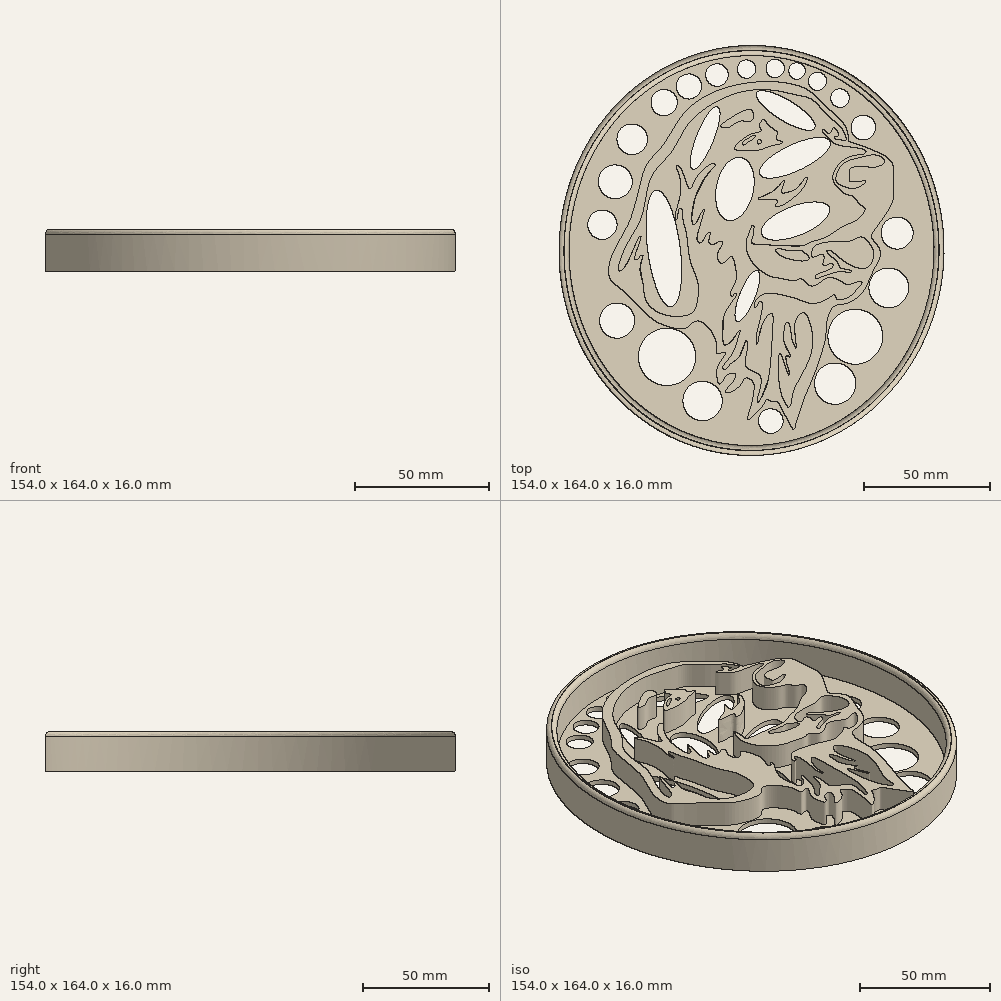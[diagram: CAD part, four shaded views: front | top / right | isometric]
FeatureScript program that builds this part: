
annotation { "Feature Type Name" : "Feature", "Feature Type Description" : "" }
export const myFeature = defineFeature(function(context is Context, id is Id, definition is map)
    precondition{}
    {
        {
            var Q0;
            Q0=qCreatedBy(makeId("Top.planeOp"),FACE);
            var sketch = newSketch(context, id + "F0", { "sketchPlane" : qUnion([Q0])});
            skFitSpline(sketch, "E0", {"points": [v(-56.75, 10.38) * mm, v(-55.7, 19.45) * mm, v(-48.18, 34.24) * mm, v(-42.3, 54.64) * mm, v(-35.83, 62.6) * mm, v(-26.27, 76.78) * mm, v(-4.51, 87.78) * mm, v(20.84, 86.33) * mm, v(30.15, 78.54) * mm, v(37.86, 70.18) * mm, v(38.92, 64.91) * mm, v(39.16, 64.77) * mm, v(51.44, 60.13) * mm, v(56.65, 55.04) * mm, v(56.67, 47.95) * mm, v(56.11, 39.8) * mm, v(48.1, 27.52) * mm, v(48.3, 25.9) * mm, v(51.21, 21.8) * mm, v(51.1, 17.66) * mm, v(48.41, 12.4) * mm, v(44.62, 4.64) * mm, v(37.98, 0) * mm, v(33.3, -1.02) * mm, v(30.35, -6.44) * mm, v(29.67, -13.3) * mm, v(28.37, -18.92) * mm, v(25.25, -28.17) * mm, v(22.14, -35.37) * mm, v(17.48, -49.26) * mm, v(17.21, -50.53) * mm, v(16.2, -49.67) * mm, v(10.7, -39.65) * mm, v(9.88, -39.14) * mm, v(8.24, -39.11) * mm, v(7.01, -38.74) * mm, v(6.11, -38.28) * mm, v(5.1, -40.2) * mm, v(-1.1, -46.46) * mm, v(-1.52, -46.2) * mm, v(0.24, -39.41) * mm, v(0.93, -34.97) * mm, v(0.79, -31.7) * mm, v(-2.1, -29.74) * mm, v(-4.25, -32.58) * mm, v(-9.22, -35.65) * mm, v(-10.48, -35.3) * mm, v(-7.7, -31.8) * mm, v(-6.36, -28.47) * mm, v(-6.93, -27.9) * mm, v(-8.8, -28.12) * mm, v(-10.72, -29.83) * mm, v(-12.3, -32.17) * mm, v(-13.36, -31.5) * mm, v(-13.78, -29.75) * mm, v(-14.02, -28.1) * mm, v(-12.93, -24.04) * mm, v(-10.29, -19.95) * mm, v(-11.11, -19.44) * mm, v(-13.52, -20.14) * mm, v(-14.12, -19.32) * mm, v(-14.33, -14.7) * mm, v(-20.48, -7.08) * mm, v(-23.89, -8.14) * mm, v(-26.78, -10) * mm, v(-36.67, -7.95) * mm, v(-42.6, -3.41) * mm, v(-52.1, 5.76) * mm, v(-56.75, 10.38) * mm]});
            skFitSpline(sketch, "E1", {"points": [v(-0.3, 77.47) * mm, v(-6.51, 75.32) * mm, v(-9.84, 73.14) * mm, v(-12.22, 70.83) * mm, v(-10.23, 70.27) * mm, v(-8.52, 70.63) * mm, v(-4.33, 73) * mm, v(-0.47, 72.84) * mm, v(0.87, 74.67) * mm, v(-0.3, 77.47) * mm]});
            skFitSpline(sketch, "E2", {"points": [v(1.36, 67.3) * mm, v(0, 66.78) * mm, v(-2.73, 65.1) * mm, v(-3.59, 63.9) * mm, v(-3.15, 63.4) * mm, v(-1.2, 64.55) * mm, v(0.65, 65.68) * mm, v(1.64, 66.8) * mm, v(1.36, 67.3) * mm]});
            skFitSpline(sketch, "E3", {"points": [v(2.68, 65.5) * mm, v(2.43, 64.42) * mm, v(3, 63.79) * mm, v(3.76, 64.1) * mm, v(4.14, 64.68) * mm, v(3.89, 65.32) * mm, v(2.68, 65.5) * mm]});
            skFitSpline(sketch, "E4", {"points": [v(4.92, 73.75) * mm, v(5.64, 72.9) * mm, v(8.3, 70.2) * mm, v(10.42, 68.26) * mm, v(10.1, 66.93) * mm, v(10.22, 65.66) * mm, v(12.07, 64.86) * mm, v(12.31, 64.26) * mm, v(8.13, 63.1) * mm, v(3.84, 61.58) * mm, v(-2.81, 61.1) * mm, v(-6.64, 61.66) * mm, v(-6.83, 62.1) * mm, v(-4.84, 64.54) * mm, v(-1.02, 67.31) * mm, v(1.75, 68.29) * mm, v(3.51, 68.7) * mm, v(3.83, 69.34) * mm, v(3.2, 70.94) * mm, v(3.87, 72.64) * mm, v(4.92, 73.75) * mm]});
            skFitSpline(sketch, "E5", {"points": [v(-52.8, 13.1) * mm, v(-53.07, 15.3) * mm, v(-49.5, 24.16) * mm, v(-44.05, 34.35) * mm, v(-41.31, 46.95) * mm, v(-37.75, 54) * mm, v(-31.73, 60.82) * mm, v(-25.59, 71.27) * mm, v(-14.26, 80.56) * mm, v(-1.6, 85.14) * mm, v(9.98, 85.18) * mm, v(17.64, 83.5) * mm, v(24.21, 81.6) * mm, v(29.93, 75.74) * mm, v(35.08, 71.25) * mm, v(37.55, 67.4) * mm, v(37.73, 65.29) * mm, v(35.6, 65.57) * mm, v(33.27, 66.1) * mm, v(33.14, 66.97) * mm, v(34.88, 66.84) * mm, v(33.65, 69.9) * mm, v(32.7, 70.35) * mm, v(31.34, 67.99) * mm, v(28.68, 69.64) * mm, v(28.46, 68.94) * mm, v(30.64, 66.33) * mm, v(33.34, 63.9) * mm, v(40.69, 62.53) * mm, v(45.7, 61.14) * mm, v(45.51, 60.03) * mm, v(40.57, 59.14) * mm, v(34.6, 55.16) * mm, v(32.53, 49.83) * mm, v(35.06, 45.82) * mm, v(38.07, 43.67) * mm, v(40.78, 42.7) * mm, v(43.35, 39.68) * mm, v(45.46, 37.86) * mm, v(42.1, 33.35) * mm, v(37.63, 31.34) * mm, v(30.07, 26.67) * mm, v(24.01, 24.63) * mm, v(20.5, 23.16) * mm, v(8.1, 23.41) * mm, v(2.64, 23.63) * mm, v(0.58, 23.93) * mm, v(0, 24.74) * mm, v(0.59, 27) * mm, v(0.84, 28.74) * mm, v(0.97, 30.82) * mm, v(0.5, 31.4) * mm, v(-0.89, 28.3) * mm, v(-2.01, 25.1) * mm, v(-1.6, 20.28) * mm, v(1.78, 14.88) * mm, v(7.61, 10.92) * mm, v(12.58, 9.94) * mm, v(17.45, 9.22) * mm, v(20.14, 9.86) * mm, v(23.27, 7.24) * mm, v(26.99, 8) * mm, v(30.9, 10.43) * mm, v(35.65, 9) * mm, v(38.66, 7.64) * mm, v(42.73, 8.71) * mm, v(44.24, 8.49) * mm, v(42.35, 5.67) * mm, v(38.8, 2.48) * mm, v(34.13, 1.86) * mm, v(33.3, 3.53) * mm, v(32.28, 3.05) * mm, v(29.8, 1.56) * mm, v(24.66, 0) * mm, v(18.49, 1.8) * mm, v(12.52, 3.4) * mm, v(7.16, 4.16) * mm, v(2.79, 2.33) * mm, v(1.12, -1.16) * mm, v(1.88, -1.4) * mm, v(3.16, 0.81) * mm, v(4.07, 0.66) * mm, v(4.2, -2.9) * mm, v(2.72, -9.21) * mm, v(1.95, -14.22) * mm, v(2.36, -16.43) * mm, v(3.13, -12.18) * mm, v(4.53, -8.19) * mm, v(6.47, -4.93) * mm, v(8.12, -4.11) * mm, v(8.64, -7.68) * mm, v(7.55, -24.3) * mm, v(5.8, -33.87) * mm, v(3.22, -39.04) * mm, v(2.62, -39.65) * mm, v(2.4, -38.5) * mm, v(3.84, -32.13) * mm, v(2.87, -28.36) * mm, v(-2.1, -25.23) * mm, v(-2.09, -20.8) * mm, v(-1.7, -15.36) * mm, v(-2.07, -14.6) * mm, v(-2.53, -15.52) * mm, v(-5.25, -21.98) * mm, v(-8.27, -24.18) * mm, v(-10.39, -26.47) * mm, v(-11.52, -25.86) * mm, v(-9.1, -22.28) * mm, v(-6.37, -17.39) * mm, v(-5.11, -13.1) * mm, v(-4.5, -10.86) * mm, v(-5.4, -11.4) * mm, v(-7.43, -14.63) * mm, v(-10.69, -16.54) * mm, v(-11.56, -13.16) * mm, v(-11.24, -5.82) * mm, v(-8.14, 0) * mm], "startDerivative": vector(-249.03, 262.65) * mm, "endDerivative": vector(350.95, 497.8) * mm});
            skFitSpline(sketch, "E6", {"points": [v(-8.14, 0) * mm, v(-6.02, 3.9) * mm, v(-6.63, 4.13) * mm, v(-7.46, 3) * mm, v(-8.37, 3.75) * mm, v(-6.48, 8.23) * mm, v(-6.47, 14.76) * mm, v(-7.96, 18.78) * mm, v(-9.76, 17.26) * mm, v(-12.25, 16.12) * mm, v(-13.67, 19.3) * mm, v(-12.16, 22.65) * mm, v(-11.55, 24.4) * mm, v(-12.45, 25) * mm, v(-14.64, 23.78) * mm, v(-16.9, 24.15) * mm, v(-16.74, 26.81) * mm, v(-16.57, 28.51) * mm, v(-17.86, 27.6) * mm, v(-20.14, 24.3) * mm, v(-21.65, 25.06) * mm, v(-21.03, 29.61) * mm, v(-19.3, 35.53) * mm, v(-18.93, 37.5) * mm, v(-20.1, 36.14) * mm, v(-21.63, 32.8) * mm, v(-23.14, 31.58) * mm, v(-23.89, 33.25) * mm, v(-21.98, 43.96) * mm, v(-16.16, 53.3) * mm, v(-14.42, 55.28) * mm, v(-14.94, 56.04) * mm, v(-17.58, 54.9) * mm, v(-22.5, 49.5) * mm, v(-24.08, 46.15) * mm, v(-24.99, 46.08) * mm, v(-27.68, 52.9) * mm, v(-29.79, 55.4) * mm, v(-29.86, 54.01) * mm, v(-28.9, 51.23) * mm, v(-28.54, 43.03) * mm, v(-30.35, 35.94) * mm, v(-30.23, 33.3) * mm, v(-29.61, 34.3) * mm, v(-29.1, 37.58) * mm, v(-28.1, 38.18) * mm, v(-27.4, 33.72) * mm, v(-26.06, 28.26) * mm, v(-24.5, 17.18) * mm, v(-21.43, 8.45) * mm, v(-21.58, 1.06) * mm, v(-24.01, -3.9) * mm, v(-35.43, -4.25) * mm, v(-42.36, 1.7) * mm, v(-43.47, 8.47) * mm, v(-44.54, 12.42) * mm, v(-44.07, 16.86) * mm, v(-43.4, 19.4) * mm, v(-44.34, 19.1) * mm, v(-45.25, 17.84) * mm, v(-46.63, 17.7) * mm, v(-44.21, 26.16) * mm, v(-44.5, 26.97) * mm, v(-48.11, 19.45) * mm, v(-50.28, 14.94) * mm, v(-52.8, 13.1) * mm], "startDerivative": vector(208.94, 286.45) * mm, "endDerivative": vector(-197.76, 76.87) * mm});
            skFitSpline(sketch, "E7", {"points": [v(45.71, 48.6) * mm, v(44.57, 47.49) * mm, v(40.55, 46.02) * mm, v(35.19, 47.65) * mm, v(33.72, 49.48) * mm, v(36.72, 55.8) * mm, v(43.76, 58.43) * mm, v(49.86, 59.4) * mm, v(53.16, 57.43) * mm, v(53.16, 56.18) * mm, v(49.61, 54.57) * mm, v(44.99, 54.85) * mm, v(42.05, 54.87) * mm, v(39.38, 53.49) * mm, v(39.15, 50.17) * mm, v(39.43, 48.86) * mm, v(41.11, 48.78) * mm, v(43.91, 48.97) * mm, v(45.41, 49.16) * mm, v(45.71, 48.6) * mm]});
            skFitSpline(sketch, "E8", {"points": [v(13.06, 49.08) * mm, v(12.67, 47.04) * mm, v(12.08, 44.35) * mm, v(14.72, 44.49) * mm, v(18.22, 46.06) * mm, v(20.69, 49.08) * mm, v(22.04, 50.55) * mm, v(22.33, 50) * mm, v(20.84, 46.35) * mm, v(16.5, 41.92) * mm, v(11.98, 39.12) * mm, v(9.7, 38.8) * mm, v(9.48, 39.47) * mm, v(10.5, 40.53) * mm, v(10.04, 41.44) * mm, v(5.26, 41.57) * mm, v(2.68, 42.04) * mm, v(4.53, 42.84) * mm, v(9.43, 45.4) * mm, v(11.8, 47.86) * mm, v(13.06, 49.08) * mm]});
            skFitSpline(sketch, "E9", {"points": [v(22.39, 17.33) * mm, v(23.15, 18.16) * mm, v(21.73, 19.91) * mm, v(19.4, 21.4) * mm, v(17, 21.1) * mm, v(15.78, 21.3) * mm, v(13.6, 21.42) * mm, v(11.44, 21.91) * mm, v(9.59, 21.33) * mm, v(11.3, 19.47) * mm, v(14.91, 17.87) * mm, v(18.51, 17.14) * mm, v(21.03, 17.05) * mm, v(22.39, 17.33) * mm]});
            skFitSpline(sketch, "E10", {"points": [v(24.3, 18.75) * mm, v(24.2, 21.1) * mm, v(26.08, 23.39) * mm, v(33.24, 24.81) * mm, v(38.8, 24.87) * mm, v(42.42, 26.27) * mm, v(44.63, 26.48) * mm, v(48.47, 21.8) * mm, v(48.7, 18.03) * mm, v(46.92, 14.7) * mm, v(43, 14.2) * mm, v(38.1, 16.21) * mm, v(33.6, 19.67) * mm, v(31.12, 21.42) * mm, v(30.11, 21.1) * mm, v(32.72, 18.16) * mm, v(34.83, 15.74) * mm, v(35.83, 14.2) * mm, v(40.03, 13.14) * mm, v(39.92, 12.39) * mm, v(36.72, 12.84) * mm, v(31.74, 11.88) * mm, v(27.23, 10.3) * mm, v(25.73, 9.92) * mm, v(25.47, 10.77) * mm, v(27.36, 12.14) * mm, v(31.06, 13.54) * mm, v(32.6, 14.82) * mm, v(32.46, 15.77) * mm, v(31.52, 15.9) * mm, v(29.96, 15.36) * mm, v(28.58, 15.66) * mm, v(28.86, 17) * mm, v(28.9, 19.25) * mm, v(28.06, 19.73) * mm, v(25.95, 18.9) * mm, v(24.3, 18.75) * mm]});
            skFitSpline(sketch, "E11", {"points": [v(15.1, -41.54) * mm, v(12.7, -38.3) * mm, v(11.16, -32.64) * mm, v(10.7, -23.74) * mm, v(11.44, -20.06) * mm, v(12.9, -23.08) * mm, v(14.38, -27.68) * mm, v(15.18, -28.68) * mm, v(14.96, -26.81) * mm, v(13.73, -21.9) * mm, v(14.3, -20.8) * mm, v(15.65, -21.62) * mm, v(15.44, -20.6) * mm, v(12.97, -15.2) * mm, v(13.06, -10.57) * mm, v(13.53, -8.24) * mm, v(14.44, -7.44) * mm, v(15.5, -9.65) * mm, v(16.24, -14.48) * mm, v(17.05, -16.45) * mm, v(17.73, -17.83) * mm, v(17.76, -15.48) * mm, v(17.28, -11.14) * mm, v(18.04, -6.07) * mm, v(20.7, -3.72) * mm, v(22.29, -5.06) * mm, v(24.45, -12.78) * mm, v(23.24, -22.04) * mm, v(18.77, -31.02) * mm, v(16.48, -36.54) * mm, v(15.1, -41.54) * mm]});
            skLineSegment(sketch, "E12.bottom", {"start": v(145.6, 60.42) * mm, "end": v(275.11, 60.42) * mm});
            skLineSegment(sketch, "E12.top", {"start": v(145.6, -89.94) * mm, "end": v(275.11, -89.94) * mm});
            skLineSegment(sketch, "E12.left", {"start": v(145.6, 60.42) * mm, "end": v(145.6, -89.94) * mm});
            skLineSegment(sketch, "E12.right", {"start": v(275.11, 60.42) * mm, "end": v(275.11, -89.94) * mm});
            skLineSegment(sketch, "E13.bottom", {"start": v(-77, 103.23) * mm, "end": v(77, 103.23) * mm});
            skLineSegment(sketch, "E13.top", {"start": v(-77, -60.77) * mm, "end": v(77, -60.77) * mm});
            skLineSegment(sketch, "E13.left", {"start": v(-77, 103.23) * mm, "end": v(-77, -60.77) * mm});
            skLineSegment(sketch, "E13.right", {"start": v(77, 103.23) * mm, "end": v(77, -60.77) * mm});
            skPoint(sketch, "E14", {"position": v(-131.67, 57.9) * mm});
            skEllipse(sketch, "E15", {"center": v(-6.64, 45.82) * mm, "majorRadius": 12.83 * mm, "minorRadius": 7.43 * mm, "majorAxis": v(-0.2, -0.98)});
            skEllipse(sketch, "E16", {"center": v(17.65, 33.01) * mm, "majorRadius": 14.54 * mm, "minorRadius": 5.91 * mm, "majorAxis": v(0.93, 0.37)});
            skEllipse(sketch, "E17", {"center": v(17.39, 58.3) * mm, "majorRadius": 15.52 * mm, "minorRadius": 5.26 * mm, "majorAxis": v(0.9, 0.43)});
            skEllipse(sketch, "E18", {"center": v(13.72, 77.22) * mm, "majorRadius": 13.55 * mm, "minorRadius": 4.17 * mm, "majorAxis": v(0.85, -0.52)});
            skEllipse(sketch, "E19", {"center": v(-1.63, 3) * mm, "majorRadius": 10.93 * mm, "minorRadius": 3.1 * mm, "majorAxis": v(-0.37, -0.93)});
            skEllipse(sketch, "E20", {"center": v(-35.05, 21.96) * mm, "majorRadius": 23.48 * mm, "minorRadius": 6.55 * mm, "majorAxis": v(0.13, -1)});
            skEllipse(sketch, "E21", {"center": v(-18.52, 66.18) * mm, "majorRadius": 13.43 * mm, "minorRadius": 3.5 * mm, "majorAxis": v(-0.37, -0.93)});
            skLineSegment(sketch, "E22", {"start": v(-73, 103.23) * mm, "end": v(-73, -60.77) * mm, "construction": true});
            skLineSegment(sketch, "E23", {"start": v(-77, 99.23) * mm, "end": v(77, 99.23) * mm, "construction": true});
            skLineSegment(sketch, "E24", {"start": v(-73, 21.23) * mm, "end": v(77, 21.23) * mm, "construction": true});
            skLineSegment(sketch, "E25", {"start": v(0, 99.23) * mm, "end": v(0, -60.77) * mm, "construction": true});
            skEllipse(sketch, "E26", {"center": v(0, 21.23) * mm, "majorRadius": 82 * mm, "minorRadius": 77 * mm, "majorAxis": v(-0.03, -1)});
            skEllipse(sketch, "E27", {"center": v(0, 21.23) * mm, "majorRadius": 78 * mm, "minorRadius": 73 * mm, "majorAxis": v(-0.03, -1)});
            skLineSegment(sketch, "E28", {"start": v(0, 116.75) * mm, "end": v(0, 115.25) * mm, "construction": true});
            skLineSegment(sketch, "E29", {"start": v(0, 103.23) * mm, "end": v(0, 116.75) * mm, "construction": true});
            skPoint(sketch, "E29.startSnap0", {"position": v(0, 103.23) * mm});
            skLineSegment(sketch, "E30", {"start": v(76.97, 19.26) * mm, "end": v(77, 21.23) * mm, "construction": true});
            skLineSegment(sketch, "E31", {"start": v(72.97, 19.36) * mm, "end": v(76.97, 19.26) * mm, "construction": true});
            skLineSegment(sketch, "E32", {"start": v(-70.26, 103.23) * mm, "end": v(-70.26, 99.23) * mm, "construction": true});
            skLineSegment(sketch, "E33", {"start": v(-77, 90.68) * mm, "end": v(-73, 90.68) * mm, "construction": true});
            skSolve(sketch);
        }
        {
            var Q0;
            Q0=makeQuery(id+"F0.imprint","IMPRINT",FACE,{"disambiguationData":[TD([[makeQuery(id+"F0.imprint","IMPRINT",EDGE,{"derivedFrom":sQuery(id+"F0.wireOp",EDGE,"E0")}),-1.0]])]});
            var Q1;
            Q1=makeQuery(id+"F0.imprint","IMPRINT",FACE,{"disambiguationData":[TD([[makeQuery(id+"F0.imprint","IMPRINT",EDGE,{"derivedFrom":sQuery(id+"F0.wireOp",EDGE,"E8")}),-1.0]])]});
            var Q2;
            Q2=makeQuery(id+"F0.imprint","IMPRINT",FACE,{"disambiguationData":[TD([[makeQuery(id+"F0.imprint","IMPRINT",EDGE,{"derivedFrom":sQuery(id+"F0.wireOp",EDGE,"E2")}),-1.0]])]});
            var Q3;
            Q3=makeQuery(id+"F0.imprint","IMPRINT",FACE,{"disambiguationData":[TD([[makeQuery(id+"F0.imprint","IMPRINT",EDGE,{"derivedFrom":sQuery(id+"F0.wireOp",EDGE,"E1")}),1.0]])]});
            extrude(context, id + "F1", {"entities" : qUnion([Q0, Q1, Q2, Q3]), "depth" : 10 * mm, "offsetDistance" : 25 * mm});
        }
        {
            var Q0;
            Q0=makeQuery(id+"F0.imprint","IMPRINT",FACE,{"disambiguationData":[TD([[makeQuery(id+"F0.imprint","IMPRINT",EDGE,{"derivedFrom":sQuery(id+"F0.wireOp",EDGE,"E0")}),1.0]])]});
            var Q1;
            Q1=makeQuery(id+"F0.imprint","IMPRINT",FACE,{"disambiguationData":[TD([[makeQuery(id+"F0.imprint","IMPRINT",EDGE,{"derivedFrom":sQuery(id+"F0.wireOp",EDGE,"E1")}),-1.0]])]});
            var Q2;
            Q2=makeQuery(id+"F0.imprint","IMPRINT",FACE,{"disambiguationData":[TD([[makeQuery(id+"F0.imprint","IMPRINT",EDGE,{"derivedFrom":sQuery(id+"F0.wireOp",EDGE,"E0")}),-1.0]])]});
            var Q3;
            Q3=makeQuery(id+"F0.imprint","IMPRINT",FACE,{"disambiguationData":[TD([[makeQuery(id+"F0.imprint","IMPRINT",EDGE,{"derivedFrom":sQuery(id+"F0.wireOp",EDGE,"E7")}),-1.0]])]});
            var Q4;
            Q4=makeQuery(id+"F0.imprint","IMPRINT",FACE,{"disambiguationData":[TD([[makeQuery(id+"F0.imprint","IMPRINT",EDGE,{"derivedFrom":sQuery(id+"F0.wireOp",EDGE,"E2")}),-1.0]])]});
            var Q5;
            Q5=makeQuery(id+"F0.imprint","IMPRINT",FACE,{"disambiguationData":[TD([[makeQuery(id+"F0.imprint","IMPRINT",EDGE,{"derivedFrom":sQuery(id+"F0.wireOp",EDGE,"E1")}),1.0]])]});
            var Q6;
            Q6=makeQuery(id+"F0.imprint","IMPRINT",FACE,{"disambiguationData":[TD([[makeQuery(id+"F0.imprint","IMPRINT",EDGE,{"derivedFrom":sQuery(id+"F0.wireOp",EDGE,"E8")}),-1.0]])]});
            var Q7;
            Q7=makeQuery(id+"F0.imprint","IMPRINT",FACE,{"disambiguationData":[TD([[makeQuery(id+"F0.imprint","IMPRINT",EDGE,{"derivedFrom":sQuery(id+"F0.wireOp",EDGE,"E3")}),1.0]])]});
            var Q8;
            Q8=makeQuery(id+"F0.imprint","IMPRINT",FACE,{"disambiguationData":[TD([[makeQuery(id+"F0.imprint","IMPRINT",EDGE,{"derivedFrom":sQuery(id+"F0.wireOp",EDGE,"E2")}),1.0]])]});
            var Q9;
            Q9=makeQuery(id+"F0.imprint","IMPRINT",FACE,{"disambiguationData":[TD([[makeQuery(id+"F0.imprint","IMPRINT",EDGE,{"derivedFrom":sQuery(id+"F0.wireOp",EDGE,"E10")}),-1.0]])]});
            var Q10;
            Q10=makeQuery(id+"F0.imprint","IMPRINT",FACE,{"disambiguationData":[TD([[makeQuery(id+"F0.imprint","IMPRINT",EDGE,{"derivedFrom":sQuery(id+"F0.wireOp",EDGE,"E11")}),-1.0]])]});
            var Q11;
            Q11=makeQuery(id+"F0.imprint","IMPRINT",FACE,{"disambiguationData":[TD([[makeQuery(id+"F0.imprint","IMPRINT",EDGE,{"derivedFrom":sQuery(id+"F0.wireOp",EDGE,"E9")}),1.0]])]});
            extrude(context, id + "F2", {"entities" : qUnion([Q0, Q1, Q2, Q3, Q4, Q5, Q6, Q7, Q8, Q9, Q10, Q11]), "operationType" : NewBodyOperationType.ADD, "oppositeDirection" : true, "depth" : 2 * mm, "offsetDistance" : 25 * mm});
        }
        {
            var Q0;
            Q0=makeQuery(id+"F0.imprint","IMPRINT",FACE,{"disambiguationData":[TD([[makeQuery(id+"F0.imprint","IMPRINT",EDGE,{"derivedFrom":sQuery(id+"F0.wireOp",EDGE,"E20")}),1.0]])]});
            var Q1;
            Q1=makeQuery(id+"F0.imprint","IMPRINT",FACE,{"disambiguationData":[TD([[makeQuery(id+"F0.imprint","IMPRINT",EDGE,{"derivedFrom":sQuery(id+"F0.wireOp",EDGE,"E21")}),1.0]])]});
            var Q2;
            Q2=makeQuery(id+"F0.imprint","IMPRINT",FACE,{"disambiguationData":[TD([[makeQuery(id+"F0.imprint","IMPRINT",EDGE,{"derivedFrom":sQuery(id+"F0.wireOp",EDGE,"E18")}),1.0]])]});
            var Q3;
            Q3=makeQuery(id+"F0.imprint","IMPRINT",FACE,{"disambiguationData":[TD([[makeQuery(id+"F0.imprint","IMPRINT",EDGE,{"derivedFrom":sQuery(id+"F0.wireOp",EDGE,"E15")}),1.0]])]});
            var Q4;
            Q4=makeQuery(id+"F0.imprint","IMPRINT",FACE,{"disambiguationData":[TD([[makeQuery(id+"F0.imprint","IMPRINT",EDGE,{"derivedFrom":sQuery(id+"F0.wireOp",EDGE,"E17")}),1.0]])]});
            var Q5;
            Q5=makeQuery(id+"F0.imprint","IMPRINT",FACE,{"disambiguationData":[TD([[makeQuery(id+"F0.imprint","IMPRINT",EDGE,{"derivedFrom":sQuery(id+"F0.wireOp",EDGE,"E16")}),1.0]])]});
            extrude(context, id + "F3", {"entities" : qUnion([Q0, Q1, Q2, Q3, Q4, Q5]), "operationType" : NewBodyOperationType.REMOVE, "oppositeDirection" : true, "depth" : 25 * mm, "offsetDistance" : 25 * mm});
        }
        {
            var Q0;
            Q0=makeQuery(id+"F0.imprint","IMPRINT",FACE,{"disambiguationData":[TD([[makeQuery(id+"F0.imprint","IMPRINT",EDGE,{"derivedFrom":sQuery(id+"F0.wireOp",EDGE,"E26")}),1.0]])]});
            extrude(context, id + "F4", {"entities" : qUnion([Q0]), "operationType" : NewBodyOperationType.ADD, "depth" : 14 * mm, "offsetDistance" : 25 * mm});
        }
        {
            var Q0;
            Q0=makeQuery(id+"F2.opExtrude","CAP_FACE",FACE,{"disambiguationData":[OSD([sQuery(id+"F0.wireOp",EDGE,"E15"),sQuery(id+"F0.wireOp",EDGE,"E16"),sQuery(id+"F0.wireOp",EDGE,"E17"),sQuery(id+"F0.wireOp",EDGE,"E18"),sQuery(id+"F0.wireOp",EDGE,"E19"),sQuery(id+"F0.wireOp",EDGE,"E20"),sQuery(id+"F0.wireOp",EDGE,"E21"),sQuery(id+"F0.wireOp",EDGE,"E27")])],"isStart":true});
            var sketch = newSketch(context, id + "F5", { "sketchPlane" : qUnion([Q0])});
            skCircle(sketch, "E34", {"center": v(-54.44, 48.7) * mm, "radius": 6.77 * mm});
            skCircle(sketch, "E35", {"center": v(-47.7, 65.68) * mm, "radius": 6.14 * mm});
            skCircle(sketch, "E36", {"center": v(-33.74, -21.34) * mm, "radius": 11.46 * mm});
            skCircle(sketch, "E37", {"center": v(41.53, -13.27) * mm, "radius": 11 * mm});
            skCircle(sketch, "E38", {"center": v(54.92, 6.27) * mm, "radius": 7.95 * mm});
            skCircle(sketch, "E39", {"center": v(58.27, 28.17) * mm, "radius": 6.4 * mm});
            skCircle(sketch, "E40", {"center": v(-19.56, -38.98) * mm, "radius": 7.87 * mm});
            skCircle(sketch, "E41", {"center": v(-53.7, -6.85) * mm, "radius": 7.03 * mm});
            skCircle(sketch, "E42", {"center": v(-59.62, 31.5) * mm, "radius": 5.86 * mm});
            skCircle(sketch, "E43", {"center": v(44.76, 70.37) * mm, "radius": 4.93 * mm});
            skCircle(sketch, "E44", {"center": v(33.48, -32.04) * mm, "radius": 8.28 * mm});
            skCircle(sketch, "E45", {"center": v(-34.94, 80.35) * mm, "radius": 5.27 * mm});
            skCircle(sketch, "E46", {"center": v(-25, 86.83) * mm, "radius": 5.02 * mm});
            skCircle(sketch, "E47", {"center": v(-13.78, 91.4) * mm, "radius": 4.52 * mm});
            skCircle(sketch, "E48", {"center": v(-1.94, 93.77) * mm, "radius": 3.69 * mm});
            skCircle(sketch, "E49", {"center": v(9.48, 94.01) * mm, "radius": 3.66 * mm});
            skCircle(sketch, "E50", {"center": v(35.42, 82.16) * mm, "radius": 3.72 * mm});
            skCircle(sketch, "E51", {"center": v(26.42, 88.85) * mm, "radius": 3.65 * mm});
            skCircle(sketch, "E52", {"center": v(18.24, 92.99) * mm, "radius": 3.31 * mm});
            skCircle(sketch, "E53", {"center": v(7.74, -47) * mm, "radius": 4.93 * mm});
            skSolve(sketch);
        }
        {
            var Q0;
            Q0=makeQuery(id+"F5.imprint","IMPRINT",FACE,{"disambiguationData":[TD([[makeQuery(id+"F5.imprint","IMPRINT",EDGE,{"derivedFrom":sQuery(id+"F5.wireOp",EDGE,"E35")}),1.0]])]});
            var Q1;
            Q1=makeQuery(id+"F5.imprint","IMPRINT",FACE,{"disambiguationData":[TD([[makeQuery(id+"F5.imprint","IMPRINT",EDGE,{"derivedFrom":sQuery(id+"F5.wireOp",EDGE,"E45")}),1.0]])]});
            var Q2;
            Q2=makeQuery(id+"F5.imprint","IMPRINT",FACE,{"disambiguationData":[TD([[makeQuery(id+"F5.imprint","IMPRINT",EDGE,{"derivedFrom":sQuery(id+"F5.wireOp",EDGE,"E46")}),1.0]])]});
            var Q3;
            Q3=makeQuery(id+"F5.imprint","IMPRINT",FACE,{"disambiguationData":[TD([[makeQuery(id+"F5.imprint","IMPRINT",EDGE,{"derivedFrom":sQuery(id+"F5.wireOp",EDGE,"E47")}),1.0]])]});
            var Q4;
            Q4=makeQuery(id+"F5.imprint","IMPRINT",FACE,{"disambiguationData":[TD([[makeQuery(id+"F5.imprint","IMPRINT",EDGE,{"derivedFrom":sQuery(id+"F5.wireOp",EDGE,"E39")}),1.0]])]});
            var Q5;
            Q5=makeQuery(id+"F5.imprint","IMPRINT",FACE,{"disambiguationData":[TD([[makeQuery(id+"F5.imprint","IMPRINT",EDGE,{"derivedFrom":sQuery(id+"F5.wireOp",EDGE,"E38")}),1.0]])]});
            var Q6;
            Q6=makeQuery(id+"F5.imprint","IMPRINT",FACE,{"disambiguationData":[TD([[makeQuery(id+"F5.imprint","IMPRINT",EDGE,{"derivedFrom":sQuery(id+"F5.wireOp",EDGE,"E37")}),1.0]])]});
            var Q7;
            Q7=makeQuery(id+"F5.imprint","IMPRINT",FACE,{"disambiguationData":[TD([[makeQuery(id+"F5.imprint","IMPRINT",EDGE,{"derivedFrom":sQuery(id+"F5.wireOp",EDGE,"E44")}),1.0]])]});
            var Q8;
            Q8=makeQuery(id+"F5.imprint","IMPRINT",FACE,{"disambiguationData":[TD([[makeQuery(id+"F5.imprint","IMPRINT",EDGE,{"derivedFrom":sQuery(id+"F5.wireOp",EDGE,"E40")}),1.0]])]});
            var Q9;
            Q9=makeQuery(id+"F5.imprint","IMPRINT",FACE,{"disambiguationData":[TD([[makeQuery(id+"F5.imprint","IMPRINT",EDGE,{"derivedFrom":sQuery(id+"F5.wireOp",EDGE,"E36")}),1.0]])]});
            var Q10;
            Q10=makeQuery(id+"F5.imprint","IMPRINT",FACE,{"disambiguationData":[TD([[makeQuery(id+"F5.imprint","IMPRINT",EDGE,{"derivedFrom":sQuery(id+"F5.wireOp",EDGE,"E41")}),1.0]])]});
            var Q11;
            Q11=makeQuery(id+"F5.imprint","IMPRINT",FACE,{"disambiguationData":[TD([[makeQuery(id+"F5.imprint","IMPRINT",EDGE,{"derivedFrom":sQuery(id+"F5.wireOp",EDGE,"E42")}),1.0]])]});
            var Q12;
            Q12=makeQuery(id+"F5.imprint","IMPRINT",FACE,{"disambiguationData":[TD([[makeQuery(id+"F5.imprint","IMPRINT",EDGE,{"derivedFrom":sQuery(id+"F5.wireOp",EDGE,"E34")}),1.0]])]});
            var Q13;
            Q13=makeQuery(id+"F5.imprint","IMPRINT",FACE,{"disambiguationData":[TD([[makeQuery(id+"F5.imprint","IMPRINT",EDGE,{"derivedFrom":sQuery(id+"F5.wireOp",EDGE,"E49")}),1.0]])]});
            var Q14;
            Q14=makeQuery(id+"F5.imprint","IMPRINT",FACE,{"disambiguationData":[TD([[makeQuery(id+"F5.imprint","IMPRINT",EDGE,{"derivedFrom":sQuery(id+"F5.wireOp",EDGE,"E48")}),1.0]])]});
            var Q15;
            Q15=makeQuery(id+"F5.imprint","IMPRINT",FACE,{"disambiguationData":[TD([[makeQuery(id+"F5.imprint","IMPRINT",EDGE,{"derivedFrom":sQuery(id+"F5.wireOp",EDGE,"E52")}),1.0]])]});
            var Q16;
            Q16=makeQuery(id+"F5.imprint","IMPRINT",FACE,{"disambiguationData":[TD([[makeQuery(id+"F5.imprint","IMPRINT",EDGE,{"derivedFrom":sQuery(id+"F5.wireOp",EDGE,"E51")}),1.0]])]});
            var Q17;
            Q17=makeQuery(id+"F5.imprint","IMPRINT",FACE,{"disambiguationData":[TD([[makeQuery(id+"F5.imprint","IMPRINT",EDGE,{"derivedFrom":sQuery(id+"F5.wireOp",EDGE,"E50")}),1.0]])]});
            var Q18;
            Q18=makeQuery(id+"F5.imprint","IMPRINT",FACE,{"disambiguationData":[TD([[makeQuery(id+"F5.imprint","IMPRINT",EDGE,{"derivedFrom":sQuery(id+"F5.wireOp",EDGE,"E43")}),1.0]])]});
            var Q19;
            Q19=makeQuery(id+"F5.imprint","IMPRINT",FACE,{"disambiguationData":[TD([[makeQuery(id+"F5.imprint","IMPRINT",EDGE,{"derivedFrom":sQuery(id+"F5.wireOp",EDGE,"E53")}),1.0]])]});
            extrude(context, id + "F6", {"entities" : qUnion([Q0, Q1, Q2, Q3, Q4, Q5, Q6, Q7, Q8, Q9, Q10, Q11, Q12, Q13, Q14, Q15, Q16, Q17, Q18, Q19]), "operationType" : NewBodyOperationType.REMOVE, "oppositeDirection" : true, "depth" : 25 * mm, "offsetDistance" : 25 * mm});
        }
        {
            var Q0;
            Q0=makeQuery(id+"F4.opExtrude","CAP_FACE",FACE,{"disambiguationData":[OSD([sQuery(id+"F0.wireOp",EDGE,"E26"),sQuery(id+"F0.wireOp",EDGE,"E27")])],"isStart":false});
            fillet(context, id + "F7", {"entities" : qUnion([Q0]), "radius" : 1.95 * mm, "tangentPropagation" : true, "allowEdgeOverflow" : false});
        }
        {
            var Q0;
            Q0=makeQuery(id+"F4.opExtrude","CAP_FACE",FACE,{"disambiguationData":[OSD([sQuery(id+"F0.wireOp",EDGE,"E26"),sQuery(id+"F0.wireOp",EDGE,"E27")])],"isStart":true});
            extrude(context, id + "F8", {"entities" : qUnion([Q0]), "operationType" : NewBodyOperationType.ADD, "depth" : 2 * mm, "offsetDistance" : 25 * mm});
        }
    });
